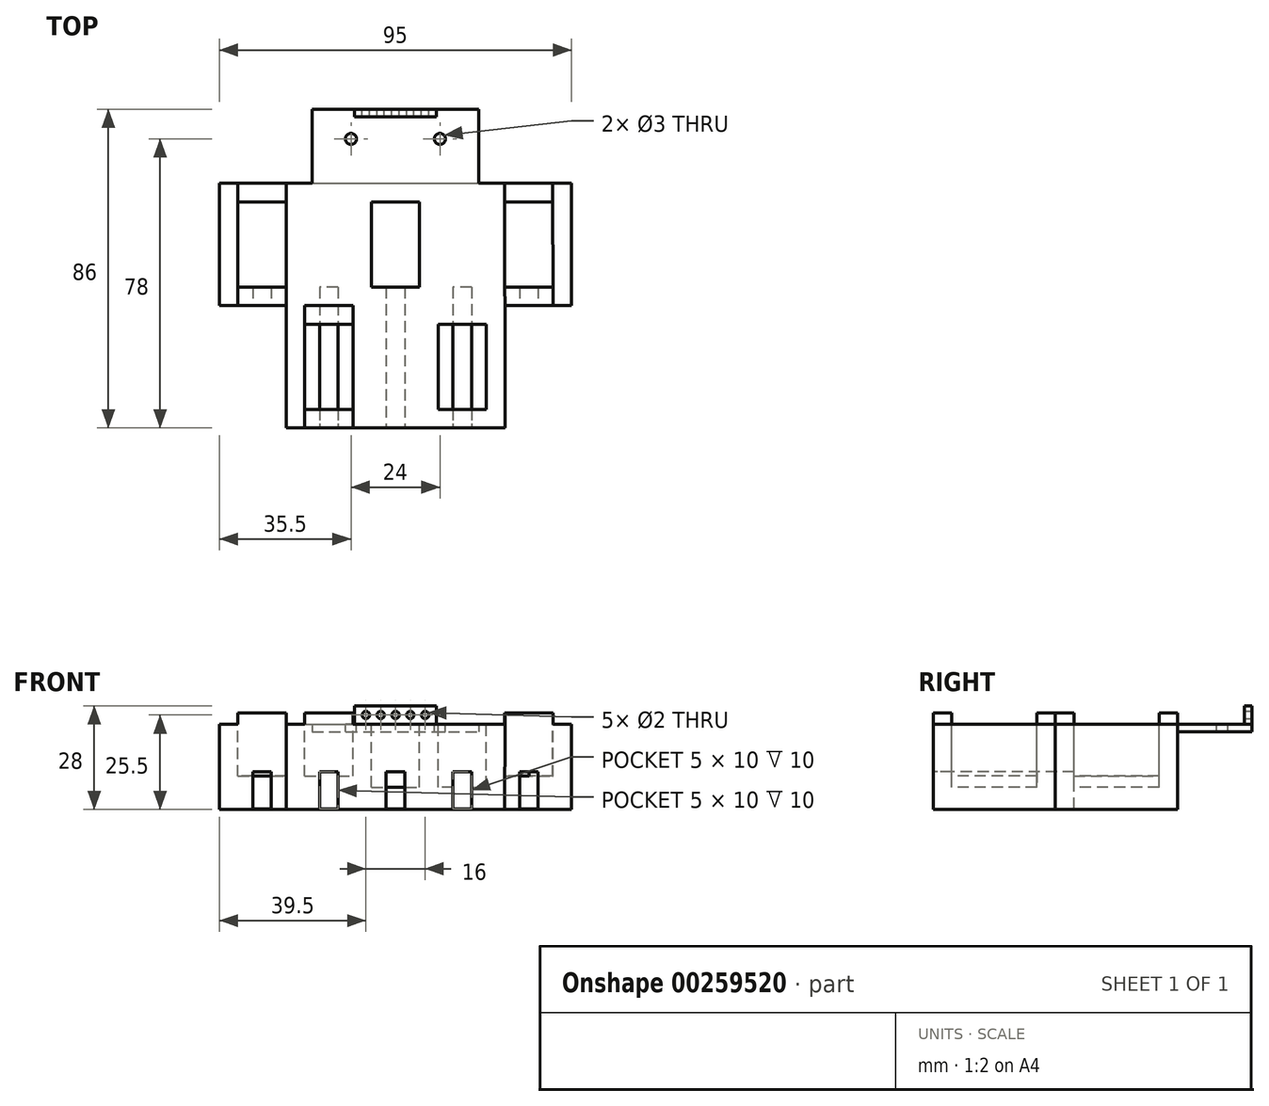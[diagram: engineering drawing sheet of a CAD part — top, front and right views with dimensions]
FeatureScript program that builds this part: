
annotation { "Feature Type Name" : "Feature", "Feature Type Description" : "" }
export const myFeature = defineFeature(function(context is Context, id is Id, definition is map)
    precondition{}
    {
        {
            var Q0;
            Q0=qCreatedBy(makeId("Front.planeOp"),FACE);
            var sketch = newSketch(context, id + "F0", { "sketchPlane" : qUnion([Q0])});
            skLineSegment(sketch, "E0", {"start": v(25, 8) * mm, "end": v(25, -8) * mm});
            skLineSegment(sketch, "E1", {"start": v(25, -8) * mm, "end": v(-25, -8) * mm});
            skLineSegment(sketch, "E2", {"start": v(-25, -8) * mm, "end": v(-25, 8) * mm});
            skLineSegment(sketch, "E3", {"start": v(-25, 8) * mm, "end": v(25, 8) * mm});
            skSolve(sketch);
        }
        {
            var Q0;
            Q0 = qSketchRegion(id + "F0", true);
            extrude(context, id + "F1", {"entities" : qUnion([Q0]), "depth" : 4 * mm});
        }
        {
            var Q0;
            Q0=makeQuery(id+"F1.opExtrude","CAP_FACE",FACE,{"disambiguationData":[OSD([sQuery(id+"F0.wireOp",EDGE,"E0"),sQuery(id+"F0.wireOp",EDGE,"E1"),sQuery(id+"F0.wireOp",EDGE,"E2"),sQuery(id+"F0.wireOp",EDGE,"E3")])],"isStart":false});
            var sketch = newSketch(context, id + "F2", { "sketchPlane" : qUnion([Q0])});
            skLineSegment(sketch, "E4.bottom", {"start": v(-47.5, -11.5) * mm, "end": v(47.5, -11.5) * mm});
            skLineSegment(sketch, "E4.top", {"start": v(-47.5, 11.5) * mm, "end": v(47.5, 11.5) * mm});
            skLineSegment(sketch, "E4.left", {"start": v(-47.5, -11.5) * mm, "end": v(-47.5, 11.5) * mm});
            skLineSegment(sketch, "E4.right", {"start": v(47.5, -11.5) * mm, "end": v(47.5, 11.5) * mm});
            skPoint(sketch, "E4.middle", {"position": v(0, 0) * mm});
            skSolve(sketch);
        }
        {
            var Q0;
            Q0 = qSketchRegion(id + "F2", true);
            extrude(context, id + "F3", {"entities" : qUnion([Q0]), "operationType" : NewBodyOperationType.ADD, "depth" : 33 * mm});
        }
        {
            var Q0;
            Q0=makeQuery(id+"F3.opExtrude","SWEPT_FACE",FACE,{"disambiguationData":[OSD([sQuery(id+"F2.wireOp",EDGE,"E4.top")])]});
            var sketch = newSketch(context, id + "F4", { "sketchPlane" : qUnion([Q0])});
            skPoint(sketch, "E5.trimOffspring.end.orphan", {"position": v(47.5, -20.5) * mm});
            skPoint(sketch, "E6.end.orphan", {"position": v(0, -37) * mm});
            skPoint(sketch, "E6.start.orphan", {"position": v(0, -4) * mm});
            skPoint(sketch, "E7.start.orphan", {"position": v(0, -20.5) * mm});
            skLineSegment(sketch, "E8", {"start": v(6.5, -32) * mm, "end": v(6.5, -9) * mm});
            skLineSegment(sketch, "E9", {"start": v(-6.5, -9) * mm, "end": v(-6.5, -32) * mm});
            skLineSegment(sketch, "E10", {"start": v(-6.5, -9) * mm, "end": v(6.5, -9) * mm});
            skLineSegment(sketch, "E11", {"start": v(-6.5, -32) * mm, "end": v(6.5, -32) * mm});
            skLineSegment(sketch, "E12", {"start": v(42.38, -9) * mm, "end": v(42.48, -31.97) * mm});
            skLineSegment(sketch, "E13", {"start": v(29.5, -22.55) * mm, "end": v(29.5, -9) * mm});
            skPoint(sketch, "E13.endSnap0", {"position": v(0, -9) * mm});
            skLineSegment(sketch, "E14", {"start": v(29.5, -22.55) * mm, "end": v(29.5, -32.03) * mm});
            skLineSegment(sketch, "E15", {"start": v(29.5, -9) * mm, "end": v(42.38, -9) * mm});
            skPoint(sketch, "E16.endSnap0", {"position": v(0, -32) * mm});
            skLineSegment(sketch, "E17", {"start": v(36, -32) * mm, "end": v(29.5, -32.03) * mm});
            skLineSegment(sketch, "E18", {"start": v(29.5, -32.03) * mm, "end": v(42.48, -31.97) * mm});
            skLineSegment(sketch, "E19", {"start": v(-35.27, -9) * mm, "end": v(-42.5, -9) * mm});
            skLineSegment(sketch, "E20", {"start": v(-42.5, -9) * mm, "end": v(-29.5, -9) * mm});
            skLineSegment(sketch, "E21", {"start": v(-29.5, -21.95) * mm, "end": v(-29.5, -9) * mm});
            skLineSegment(sketch, "E22", {"start": v(-35.5, -32) * mm, "end": v(-29.5, -32) * mm});
            skLineSegment(sketch, "E23", {"start": v(-35.5, -32) * mm, "end": v(-42.5, -32) * mm});
            skLineSegment(sketch, "E24", {"start": v(-42.5, -32) * mm, "end": v(-42.5, -21.71) * mm});
            skLineSegment(sketch, "E25", {"start": v(-42.5, -21.71) * mm, "end": v(-42.5, -9) * mm});
            skLineSegment(sketch, "E26", {"start": v(-29.5, -21.95) * mm, "end": v(-29.5, -32) * mm});
            skSolve(sketch);
        }
        {
            var Q0;
            Q0=makeQuery(id+"F4.imprint","IMPRINT",FACE,{"disambiguationData":[TD([[makeQuery(id+"F4.imprint","IMPRINT",EDGE,{"derivedFrom":sQuery(id+"F4.wireOp",EDGE,"E8")}),1.0]])]});
            extrude(context, id + "F5", {"entities" : qUnion([Q0]), "operationType" : NewBodyOperationType.REMOVE, "oppositeDirection" : true, "depth" : 17 * mm});
        }
        {
            var Q0;
            {var subQ0=sQuery(id+"F4.wireOp",EDGE,"E21");Q0=makeQuery(id+"F4.imprint","IMPRINT",FACE,{"disambiguationData":[TD([[makeQuery(id+"F4.imprint","IMPRINT",EDGE,{"derivedFrom":subQ0}),1.0]])]});}
            extrude(context, id + "F6", {"entities" : qUnion([Q0]), "operationType" : NewBodyOperationType.REMOVE, "oppositeDirection" : true, "depth" : 14 * mm});
        }
        {
            var Q0;
            {var subQ1=sQuery(id+"F4.wireOp",EDGE,"E12");Q0=makeQuery(id+"F4.imprint","IMPRINT",FACE,{"disambiguationData":[TD([[makeQuery(id+"F4.imprint","IMPRINT",EDGE,{"derivedFrom":subQ1}),-1.0]])]});}
            extrude(context, id + "F7", {"entities" : qUnion([Q0]), "operationType" : NewBodyOperationType.REMOVE, "oppositeDirection" : true, "depth" : 14 * mm});
        }
        {
            var Q0;
            Q0=makeQuery(id+"F3.opExtrude","SWEPT_FACE",FACE,{"disambiguationData":[OSD([sQuery(id+"F2.wireOp",EDGE,"E4.top")])]});
            var sketch = newSketch(context, id + "F8", { "sketchPlane" : qUnion([Q0])});
            skLineSegment(sketch, "E27", {"start": v(-29.5, -9) * mm, "end": v(-29.5, -4) * mm});
            skLineSegment(sketch, "E28", {"start": v(-42.5, -9) * mm, "end": v(-42.5, -4) * mm});
            skLineSegment(sketch, "E29", {"start": v(-29.5, -32) * mm, "end": v(-29.5, -37) * mm});
            skLineSegment(sketch, "E30", {"start": v(-42.5, -32) * mm, "end": v(-42.5, -37) * mm});
            skLineSegment(sketch, "E31", {"start": v(29.5, -9) * mm, "end": v(29.5, -4) * mm});
            skLineSegment(sketch, "E32", {"start": v(42.38, -9) * mm, "end": v(42.38, -4) * mm});
            skLineSegment(sketch, "E33", {"start": v(29.5, -32.03) * mm, "end": v(29.52, -37) * mm});
            skLineSegment(sketch, "E34", {"start": v(42.48, -31.97) * mm, "end": v(42.5, -37) * mm});
            skSolve(sketch);
        }
        {
            var Q0;
            {var subQ0=sQuery(id+"F8.wireOp",EDGE,"E27");Q0=makeQuery(id+"F8.imprint","IMPRINT",FACE,{"disambiguationData":[TD([[makeQuery(id+"F8.imprint","IMPRINT",EDGE,{"derivedFrom":subQ0}),1.0]])]});}
            var Q1;
            {var subQ0=sQuery(id+"F8.wireOp",EDGE,"E29");Q1=makeQuery(id+"F8.imprint","IMPRINT",FACE,{"disambiguationData":[TD([[makeQuery(id+"F8.imprint","IMPRINT",EDGE,{"derivedFrom":subQ0}),-1.0]])]});}
            var Q2;
            {var subQ0=sQuery(id+"F8.wireOp",EDGE,"E31");Q2=makeQuery(id+"F8.imprint","IMPRINT",FACE,{"disambiguationData":[TD([[makeQuery(id+"F8.imprint","IMPRINT",EDGE,{"derivedFrom":subQ0}),-1.0]])]});}
            var Q3;
            {var subQ0=sQuery(id+"F8.wireOp",EDGE,"E33");Q3=makeQuery(id+"F8.imprint","IMPRINT",FACE,{"disambiguationData":[TD([[makeQuery(id+"F8.imprint","IMPRINT",EDGE,{"derivedFrom":subQ0}),1.0]])]});}
            extrude(context, id + "F9", {"entities" : qUnion([Q0, Q1, Q2, Q3]), "operationType" : NewBodyOperationType.ADD, "depth" : 3 * mm});
        }
        {
            var Q0;
            Q0=makeQuery(id+"F1.opExtrude","CAP_FACE",FACE,{"disambiguationData":[OSD([sQuery(id+"F0.wireOp",EDGE,"E0"),sQuery(id+"F0.wireOp",EDGE,"E1"),sQuery(id+"F0.wireOp",EDGE,"E2"),sQuery(id+"F0.wireOp",EDGE,"E3")])],"isStart":true});
            var sketch = newSketch(context, id + "F10", { "sketchPlane" : qUnion([Q0])});
            skLineSegment(sketch, "E35.0.0", {"start": v(25, 8) * mm, "end": v(-25, 8) * mm});
            skLineSegment(sketch, "E35.0.1", {"start": v(-25, 8) * mm, "end": v(-25, -8) * mm});
            skLineSegment(sketch, "E35.0.2", {"start": v(-25, -8) * mm, "end": v(25, -8) * mm});
            skLineSegment(sketch, "E35.0.3", {"start": v(25, -8) * mm, "end": v(25, 8) * mm});
            skSolve(sketch);
        }
        {
            var Q0;
            Q0=makeQuery(id+"F10.imprint","IMPRINT",FACE,{"disambiguationData":[TD([[makeQuery(id+"F10.imprint","IMPRINT",EDGE,{"derivedFrom":sQuery(id+"F10.wireOp",EDGE,"E35.0.0")}),1.0]])]});
            var Q1;
            {var subQ0=sQuery(id+"F2.wireOp",EDGE,"E4.top");var subQ1=makeQuery(id+"F3.opExtrude","CAP_EDGE",EDGE,{"disambiguationData":[OSD([subQ0])],"isStart":true});Q1=makeQuery(id+"F9.boolean.opBoolean","MERGE",FACE,{"derivedFrom":[makeQuery(id+"F3.opExtrude","CAP_FACE",FACE,{"disambiguationData":[OSD([sQuery(id+"F2.wireOp",EDGE,"E4.bottom"),subQ0,sQuery(id+"F2.wireOp",EDGE,"E4.left"),sQuery(id+"F2.wireOp",EDGE,"E4.right")])],"isStart":true}),makeQuery(id+"F9.opExtrude","SWEPT_FACE",FACE,{"disambiguationData":[OSD([subQ0]),TDD([makeQuery(id+"F8.imprint","IMPRINT",EDGE,{"disambiguationData":[TD([[makeQuery(id+"F8.imprint","INTERSECT",VERTEX,{"derivedFrom":[subQ1,sQuery(id+"F8.wireOp",EDGE,"E27")]}),1.0]])],"derivedFrom":subQ1})])]}),makeQuery(id+"F9.opExtrude","SWEPT_FACE",FACE,{"disambiguationData":[OSD([subQ0]),TDD([makeQuery(id+"F8.imprint","IMPRINT",EDGE,{"disambiguationData":[TD([[makeQuery(id+"F8.imprint","INTERSECT",VERTEX,{"derivedFrom":[subQ1,sQuery(id+"F8.wireOp",EDGE,"E31")]}),-1.0]])],"derivedFrom":subQ1})])]})]});}
            extrude(context, id + "F11", {"entities" : qUnion([Q0]), "operationType" : NewBodyOperationType.REMOVE, "endBound" : BoundingType.UP_TO_SURFACE, "oppositeDirection" : true, "endBoundEntityFace" : qUnion([Q1]), "depth" : 25 * mm});
        }
        {
            var Q0;
            {var subQ0=sQuery(id+"F2.wireOp",EDGE,"E4.right");var subQ1=sQuery(id+"F2.wireOp",EDGE,"E4.left");var subQ2=sQuery(id+"F2.wireOp",EDGE,"E4.top");var subQ3=sQuery(id+"F2.wireOp",EDGE,"E4.bottom");var subQ4=makeQuery(id+"F3.opExtrude","CAP_EDGE",EDGE,{"disambiguationData":[OSD([subQ2])],"isStart":true});Q0=makeQuery(id+"F11.boolean.opBoolean","MERGE",FACE,{"derivedFrom":[makeQuery(id+"F9.boolean.opBoolean","MERGE",FACE,{"derivedFrom":[makeQuery(id+"F3.opExtrude","CAP_FACE",FACE,{"disambiguationData":[OSD([subQ3,subQ2,subQ1,subQ0])],"isStart":true}),makeQuery(id+"F9.opExtrude","SWEPT_FACE",FACE,{"disambiguationData":[OSD([subQ2]),TDD([makeQuery(id+"F8.imprint","IMPRINT",EDGE,{"disambiguationData":[TD([[makeQuery(id+"F8.imprint","INTERSECT",VERTEX,{"derivedFrom":[subQ4,sQuery(id+"F8.wireOp",EDGE,"E27")]}),1.0]])],"derivedFrom":subQ4})])]}),makeQuery(id+"F9.opExtrude","SWEPT_FACE",FACE,{"disambiguationData":[OSD([subQ2]),TDD([makeQuery(id+"F8.imprint","IMPRINT",EDGE,{"disambiguationData":[TD([[makeQuery(id+"F8.imprint","INTERSECT",VERTEX,{"derivedFrom":[subQ4,sQuery(id+"F8.wireOp",EDGE,"E31")]}),-1.0]])],"derivedFrom":subQ4})])]})]}),makeQuery(id+"F11.opExtrude","CAP_FACE",FACE,{"disambiguationData":[OSD([subQ3,subQ2,subQ1,subQ0])],"isStart":false})]});}
            var sketch = newSketch(context, id + "F12", { "sketchPlane" : qUnion([Q0])});
            skLineSegment(sketch, "E36", {"start": v(0, -11.5) * mm, "end": v(22.5, -11.5) * mm});
            skLineSegment(sketch, "E37", {"start": v(0, -11.5) * mm, "end": v(-22.5, -11.5) * mm});
            skLineSegment(sketch, "E38", {"start": v(-22.5, -11.5) * mm, "end": v(-22.5, -9.5) * mm});
            skLineSegment(sketch, "E39", {"start": v(22.5, -11.5) * mm, "end": v(22.5, -9.5) * mm});
            skLineSegment(sketch, "E40", {"start": v(22.5, -9.5) * mm, "end": v(-22.5, -9.5) * mm});
            skLineSegment(sketch, "E41.MirrorCS", {"start": v(22.5, 9.5) * mm, "end": v(-22.5, 9.5) * mm});
            skLineSegment(sketch, "E42.MirrorCS", {"start": v(0, 11.5) * mm, "end": v(22.5, 11.5) * mm});
            skLineSegment(sketch, "E43.MirrorCS", {"start": v(22.5, 11.5) * mm, "end": v(22.5, 9.5) * mm});
            skLineSegment(sketch, "E44.MirrorCS", {"start": v(0, 11.5) * mm, "end": v(-22.5, 11.5) * mm});
            skLineSegment(sketch, "E45.MirrorCS", {"start": v(-22.5, 11.5) * mm, "end": v(-22.5, 9.5) * mm});
            skSolve(sketch);
        }
        {
            var Q0;
            Q0=makeQuery(id+"F12.imprint","IMPRINT",FACE,{"disambiguationData":[TD([[makeQuery(id+"F12.imprint","IMPRINT",EDGE,{"derivedFrom":sQuery(id+"F12.wireOp",EDGE,"E41.MirrorCS")}),-1.0]])]});
            extrude(context, id + "F13", {"entities" : qUnion([Q0]), "operationType" : NewBodyOperationType.ADD, "depth" : 20 * mm});
        }
        {
            var Q0;
            {var subQ0=sQuery(id+"F2.wireOp",EDGE,"E4.top");var subQ1=makeQuery(id+"F3.opExtrude","CAP_EDGE",EDGE,{"disambiguationData":[OSD([subQ0])],"isStart":false});Q0=makeQuery(id+"F9.boolean.opBoolean","MERGE",FACE,{"derivedFrom":[makeQuery(id+"F3.opExtrude","CAP_FACE",FACE,{"disambiguationData":[OSD([sQuery(id+"F2.wireOp",EDGE,"E4.bottom"),subQ0,sQuery(id+"F2.wireOp",EDGE,"E4.left"),sQuery(id+"F2.wireOp",EDGE,"E4.right")])],"isStart":false}),makeQuery(id+"F9.opExtrude","SWEPT_FACE",FACE,{"disambiguationData":[OSD([subQ0]),TDD([makeQuery(id+"F8.imprint","IMPRINT",EDGE,{"disambiguationData":[TD([[makeQuery(id+"F8.imprint","INTERSECT",VERTEX,{"derivedFrom":[subQ1,sQuery(id+"F8.wireOp",EDGE,"E29")]}),1.0]])],"derivedFrom":subQ1})])]}),makeQuery(id+"F9.opExtrude","SWEPT_FACE",FACE,{"disambiguationData":[OSD([subQ0]),TDD([makeQuery(id+"F8.imprint","IMPRINT",EDGE,{"disambiguationData":[TD([[makeQuery(id+"F8.imprint","INTERSECT",VERTEX,{"derivedFrom":[subQ1,sQuery(id+"F8.wireOp",EDGE,"E33")]}),-1.0]])],"derivedFrom":subQ1})])]})]});}
            var sketch = newSketch(context, id + "F14", { "sketchPlane" : qUnion([Q0])});
            skLineSegment(sketch, "E46", {"start": v(0, -11.5) * mm, "end": v(-29.5, -11.5) * mm});
            skLineSegment(sketch, "E47", {"start": v(0, -11.5) * mm, "end": v(29.5, -11.5) * mm});
            skLineSegment(sketch, "E48", {"start": v(-29.5, -11.5) * mm, "end": v(-29.5, 11.5) * mm});
            skLineSegment(sketch, "E49", {"start": v(29.5, -11.5) * mm, "end": v(29.52, 11.5) * mm});
            skSolve(sketch);
        }
        {
            var Q0;
            Q0=makeQuery(id+"F14.imprint","IMPRINT",FACE,{"disambiguationData":[TD([[makeQuery(id+"F14.imprint","IMPRINT",EDGE,{"derivedFrom":sQuery(id+"F14.wireOp",EDGE,"E46")}),1.0]])]});
            extrude(context, id + "F15", {"entities" : qUnion([Q0]), "operationType" : NewBodyOperationType.ADD, "depth" : 33 * mm});
        }
        {
            var Q0;
            {var subQ0=sQuery(id+"F2.wireOp",EDGE,"E4.top");Q0=makeQuery(id+"F15.boolean.opBoolean","MERGE",FACE,{"derivedFrom":[makeQuery(id+"F9.boolean.opBoolean","SPLIT",FACE,{"disambiguationData":[TD([makeQuery(id+"F5.boolean.opBoolean","COPY",FACE,{"derivedFrom":makeQuery(id+"F5.opExtrude","SWEPT_FACE",FACE,{"disambiguationData":[OSD([sQuery(id+"F4.wireOp",EDGE,"E8")])]})})])],"derivedFrom":makeQuery(id+"F3.opExtrude","SWEPT_FACE",FACE,{"disambiguationData":[OSD([subQ0])]})}),makeQuery(id+"F15.opExtrude","SWEPT_FACE",FACE,{"disambiguationData":[OSD([subQ0])]})]});}
            var sketch = newSketch(context, id + "F16", { "sketchPlane" : qUnion([Q0])});
            skLineSegment(sketch, "E50", {"start": v(-17.67, -65) * mm, "end": v(-24.5, -65) * mm});
            skLineSegment(sketch, "E51", {"start": v(-17.67, -65) * mm, "end": v(-11.5, -65) * mm});
            skLineSegment(sketch, "E52", {"start": v(-11.5, -54.94) * mm, "end": v(-11.5, -65) * mm});
            skLineSegment(sketch, "E53", {"start": v(-24.5, -55.7) * mm, "end": v(-24.5, -65) * mm});
            skLineSegment(sketch, "E54", {"start": v(-18.18, -42) * mm, "end": v(-24.5, -42) * mm});
            skLineSegment(sketch, "E55", {"start": v(-18.18, -42) * mm, "end": v(-11.5, -42) * mm});
            skLineSegment(sketch, "E56", {"start": v(-11.5, -54.94) * mm, "end": v(-11.5, -42) * mm});
            skLineSegment(sketch, "E57", {"start": v(-24.5, -55.7) * mm, "end": v(-24.5, -42) * mm});
            skLineSegment(sketch, "E58", {"start": v(17.15, -42) * mm, "end": v(11.5, -42) * mm});
            skLineSegment(sketch, "E59", {"start": v(17.15, -42) * mm, "end": v(24.52, -42) * mm});
            skLineSegment(sketch, "E60", {"start": v(19.42, -65) * mm, "end": v(11.5, -65) * mm});
            skLineSegment(sketch, "E61", {"start": v(19.42, -65) * mm, "end": v(24.52, -65) * mm});
            skLineSegment(sketch, "E62", {"start": v(11.5, -54.94) * mm, "end": v(11.5, -65) * mm});
            skLineSegment(sketch, "E63", {"start": v(24.52, -53.5) * mm, "end": v(24.52, -65) * mm});
            skLineSegment(sketch, "E64", {"start": v(11.5, -54.94) * mm, "end": v(11.5, -42) * mm});
            skLineSegment(sketch, "E65", {"start": v(24.52, -53.5) * mm, "end": v(24.52, -42) * mm});
            skPoint(sketch, "E66.start.orphan", {"position": v(29.52, -53.5) * mm});
            skPoint(sketch, "E67.start.orphan", {"position": v(0, -70) * mm});
            skSolve(sketch);
        }
        {
            var Q0;
            Q0=makeQuery(id+"F16.imprint","IMPRINT",FACE,{"disambiguationData":[TD([[makeQuery(id+"F16.imprint","IMPRINT",EDGE,{"derivedFrom":sQuery(id+"F16.wireOp",EDGE,"E50")}),-1.0]])]});
            extrude(context, id + "F17", {"entities" : qUnion([Q0]), "operationType" : NewBodyOperationType.REMOVE, "oppositeDirection" : true, "depth" : 14 * mm});
        }
        {
            var Q0;
            Q0=makeQuery(id+"F16.imprint","IMPRINT",FACE,{"disambiguationData":[TD([[makeQuery(id+"F16.imprint","IMPRINT",EDGE,{"derivedFrom":sQuery(id+"F16.wireOp",EDGE,"E58")}),1.0]])]});
            extrude(context, id + "F18", {"entities" : qUnion([Q0]), "operationType" : NewBodyOperationType.REMOVE, "oppositeDirection" : true, "depth" : 17 * mm});
        }
        {
            var Q0;
            {var subQ0=sQuery(id+"F2.wireOp",EDGE,"E4.top");Q0=makeQuery(id+"F15.boolean.opBoolean","MERGE",FACE,{"derivedFrom":[makeQuery(id+"F9.boolean.opBoolean","SPLIT",FACE,{"disambiguationData":[TD([makeQuery(id+"F5.boolean.opBoolean","COPY",FACE,{"derivedFrom":makeQuery(id+"F5.opExtrude","SWEPT_FACE",FACE,{"disambiguationData":[OSD([sQuery(id+"F4.wireOp",EDGE,"E8")])]})})])],"derivedFrom":makeQuery(id+"F3.opExtrude","SWEPT_FACE",FACE,{"disambiguationData":[OSD([subQ0])]})}),makeQuery(id+"F15.opExtrude","SWEPT_FACE",FACE,{"disambiguationData":[OSD([subQ0])]})]});}
            var sketch = newSketch(context, id + "F19", { "sketchPlane" : qUnion([Q0])});
            skLineSegment(sketch, "E68", {"start": v(-24.5, -42) * mm, "end": v(-24.5, -37) * mm});
            skLineSegment(sketch, "E69", {"start": v(-24.5, -37) * mm, "end": v(-11.5, -37) * mm});
            skLineSegment(sketch, "E70", {"start": v(-11.5, -37) * mm, "end": v(-11.5, -42) * mm});
            skLineSegment(sketch, "E71", {"start": v(-24.5, -65) * mm, "end": v(-24.5, -70) * mm});
            skLineSegment(sketch, "E72", {"start": v(-11.5, -65) * mm, "end": v(-11.5, -70) * mm});
            skSolve(sketch);
        }
        {
            var Q0;
            {var subQ0=sQuery(id+"F19.wireOp",EDGE,"E71");Q0=makeQuery(id+"F19.imprint","IMPRINT",FACE,{"disambiguationData":[TD([[makeQuery(id+"F19.imprint","IMPRINT",EDGE,{"derivedFrom":subQ0}),1.0]])]});}
            var Q1;
            Q1=makeQuery(id+"F19.imprint","IMPRINT",FACE,{"disambiguationData":[TD([[makeQuery(id+"F19.imprint","IMPRINT",EDGE,{"derivedFrom":sQuery(id+"F19.wireOp",EDGE,"E68")}),-1.0]])]});
            extrude(context, id + "F20", {"entities" : qUnion([Q0, Q1]), "operationType" : NewBodyOperationType.ADD, "depth" : 3 * mm});
        }
        {
            var Q0;
            {var subQ0=sQuery(id+"F2.wireOp",EDGE,"E4.top");Q0=makeQuery(id+"F15.boolean.opBoolean","MERGE",FACE,{"derivedFrom":[makeQuery(id+"F13.boolean.opBoolean","MERGE",FACE,{"derivedFrom":[makeQuery(id+"F9.boolean.opBoolean","SPLIT",FACE,{"disambiguationData":[TD([makeQuery(id+"F5.boolean.opBoolean","COPY",FACE,{"derivedFrom":makeQuery(id+"F5.opExtrude","SWEPT_FACE",FACE,{"disambiguationData":[OSD([sQuery(id+"F4.wireOp",EDGE,"E8")])]})})])],"derivedFrom":makeQuery(id+"F3.opExtrude","SWEPT_FACE",FACE,{"disambiguationData":[OSD([subQ0])]})}),makeQuery(id+"F13.opExtrude","SWEPT_FACE",FACE,{"disambiguationData":[OSD([sQuery(id+"F12.wireOp",EDGE,"E42.MirrorCS"),sQuery(id+"F12.wireOp",EDGE,"E44.MirrorCS")])]})]}),makeQuery(id+"F15.opExtrude","SWEPT_FACE",FACE,{"disambiguationData":[OSD([subQ0])]})]});}
            var sketch = newSketch(context, id + "F21", { "sketchPlane" : qUnion([Q0])});
            skCircle(sketch, "E73", {"center": v(-12, 8) * mm, "radius": 1.5 * mm});
            skCircle(sketch, "E74.MirrorC", {"center": v(12, 8) * mm, "radius": 1.5 * mm});
            skSolve(sketch);
        }
        {
            var Q0;
            Q0 = qSketchRegion(id + "F21", true);
            extrude(context, id + "F22", {"entities" : qUnion([Q0]), "operationType" : NewBodyOperationType.REMOVE, "endBound" : BoundingType.THROUGH_ALL, "oppositeDirection" : true, "depth" : 25 * mm});
        }
        {
            var Q0;
            {var subQ0=sQuery(id+"F2.wireOp",EDGE,"E4.top");Q0=makeQuery(id+"F20.boolean.opBoolean","MERGE",FACE,{"derivedFrom":[makeQuery(id+"F15.opExtrude","CAP_FACE",FACE,{"disambiguationData":[OSD([subQ0,sQuery(id+"F14.wireOp",EDGE,"E46"),sQuery(id+"F14.wireOp",EDGE,"E47"),sQuery(id+"F14.wireOp",EDGE,"E48"),sQuery(id+"F14.wireOp",EDGE,"E49")])],"isStart":false}),makeQuery(id+"F20.opExtrude","SWEPT_FACE",FACE,{"disambiguationData":[OSD([subQ0])]})]});}
            var sketch = newSketch(context, id + "F23", { "sketchPlane" : qUnion([Q0])});
            skLineSegment(sketch, "E75.bottom", {"start": v(-20.5, -1.3) * mm, "end": v(-15.5, -1.3) * mm});
            skLineSegment(sketch, "E75.top", {"start": v(-20.5, -11.3) * mm, "end": v(-15.5, -11.3) * mm});
            skLineSegment(sketch, "E75.left", {"start": v(-20.5, -1.3) * mm, "end": v(-20.5, -11.3) * mm});
            skLineSegment(sketch, "E75.right", {"start": v(-15.5, -1.3) * mm, "end": v(-15.5, -11.3) * mm});
            skPoint(sketch, "E75.middle", {"position": v(-18, -6.3) * mm});
            skPoint(sketch, "E75.middle.positionSnap0", {"position": v(-18, 14.5) * mm});
            skPoint(sketch, "E75.centerSnap0", {"position": v(-18, 14.5) * mm});
            skLineSegment(sketch, "E76.bottom", {"start": v(-2.5, -1.3) * mm, "end": v(2.5, -1.3) * mm});
            skLineSegment(sketch, "E76.top", {"start": v(-2.5, -11.3) * mm, "end": v(2.5, -11.3) * mm});
            skLineSegment(sketch, "E76.left", {"start": v(-2.5, -1.3) * mm, "end": v(-2.5, -11.3) * mm});
            skLineSegment(sketch, "E76.right", {"start": v(2.5, -1.3) * mm, "end": v(2.5, -11.3) * mm});
            skPoint(sketch, "E76.middle", {"position": v(0, -6.3) * mm});
            skPoint(sketch, "E76.middle.positionSnap0", {"position": v(-15.5, -6.3) * mm});
            skPoint(sketch, "E76.centerSnap0", {"position": v(-15.5, -6.3) * mm});
            skLineSegment(sketch, "E77.bottom", {"start": v(15.51, -1.3) * mm, "end": v(20.51, -1.3) * mm});
            skLineSegment(sketch, "E77.top", {"start": v(15.51, -11.3) * mm, "end": v(20.51, -11.3) * mm});
            skLineSegment(sketch, "E77.left", {"start": v(15.51, -1.3) * mm, "end": v(15.51, -11.3) * mm});
            skLineSegment(sketch, "E77.right", {"start": v(20.51, -1.3) * mm, "end": v(20.51, -11.3) * mm});
            skPoint(sketch, "E77.middle", {"position": v(18.01, -6.3) * mm});
            skPoint(sketch, "E77.middle.positionSnap0", {"position": v(18.01, -5.5) * mm});
            skPoint(sketch, "E77.centerSnap0", {"position": v(18.01, -5.5) * mm});
            skLineSegment(sketch, "E78.0.0", {"start": v(-29.5, 14.5) * mm, "end": v(-42.5, 14.5) * mm});
            skLineSegment(sketch, "E78.0.2", {"start": v(-42.5, 14.5) * mm, "end": v(-29.5, 14.5) * mm});
            skLineSegment(sketch, "E79.bottom", {"start": v(-33.5, -1.3) * mm, "end": v(-38.5, -1.3) * mm});
            skLineSegment(sketch, "E79.top", {"start": v(-33.5, -11.3) * mm, "end": v(-38.5, -11.3) * mm});
            skLineSegment(sketch, "E79.left", {"start": v(-33.5, -1.3) * mm, "end": v(-33.5, -11.3) * mm});
            skLineSegment(sketch, "E79.right", {"start": v(-38.5, -1.3) * mm, "end": v(-38.5, -11.3) * mm});
            skPoint(sketch, "E79.middle", {"position": v(-36, -6.3) * mm});
            skPoint(sketch, "E79.middle.positionSnap0", {"position": v(-36, 14.5) * mm});
            skPoint(sketch, "E79.centerSnap0", {"position": v(-36, 14.5) * mm});
            skLineSegment(sketch, "E80.MirrorCS", {"start": v(38.5, -1.3) * mm, "end": v(38.5, -11.3) * mm});
            skLineSegment(sketch, "E81.MirrorCS", {"start": v(33.5, -1.3) * mm, "end": v(38.5, -1.3) * mm});
            skLineSegment(sketch, "E82.MirrorCS", {"start": v(33.5, -1.3) * mm, "end": v(33.5, -11.3) * mm});
            skLineSegment(sketch, "E83.MirrorCS", {"start": v(33.5, -11.3) * mm, "end": v(38.5, -11.3) * mm});
            skPoint(sketch, "E84.0.6.end.orphan", {"position": v(29.52, 11.5) * mm});
            skPoint(sketch, "E84.0.5.end.orphan", {"position": v(29.52, 14.5) * mm});
            skPoint(sketch, "E84.0.1.start.orphan", {"position": v(29.5, -11.5) * mm});
            skPoint(sketch, "E84.0.2.start.orphan", {"position": v(47.5, -11.5) * mm});
            skPoint(sketch, "E84.0.3.start.orphan", {"position": v(47.5, 11.5) * mm});
            skPoint(sketch, "E84.0.4.end.orphan", {"position": v(42.5, 14.5) * mm});
            skPoint(sketch, "E84.0.4.start.orphan", {"position": v(42.5, 11.5) * mm});
            skSolve(sketch);
        }
        {
            var Q0;
            Q0 = qSketchRegion(id + "F23", true);
            var Q1;
            Q1=makeQuery(id+"F5.boolean.opBoolean","COPY",FACE,{"derivedFrom":makeQuery(id+"F5.opExtrude","SWEPT_FACE",FACE,{"disambiguationData":[OSD([sQuery(id+"F4.wireOp",EDGE,"E11")])]})});
            extrude(context, id + "F24", {"entities" : qUnion([Q0]), "operationType" : NewBodyOperationType.REMOVE, "endBound" : BoundingType.UP_TO_SURFACE, "oppositeDirection" : true, "endBoundEntityFace" : qUnion([Q1]), "depth" : 25 * mm});
        }
        {
            var Q0;
            Q0=makeQuery(id+"F13.opExtrude","CAP_FACE",FACE,{"disambiguationData":[OSD([sQuery(id+"F12.wireOp",EDGE,"E41.MirrorCS"),sQuery(id+"F12.wireOp",EDGE,"E42.MirrorCS"),sQuery(id+"F12.wireOp",EDGE,"E43.MirrorCS"),sQuery(id+"F12.wireOp",EDGE,"E44.MirrorCS"),sQuery(id+"F12.wireOp",EDGE,"E45.MirrorCS")])],"isStart":false});
            var sketch = newSketch(context, id + "F25", { "sketchPlane" : qUnion([Q0])});
            skCircle(sketch, "E85", {"center": v(0, 14) * mm, "radius": 1 * mm});
            skCircle(sketch, "E86.1.0.0", {"center": v(4, 14) * mm, "radius": 1 * mm});
            skCircle(sketch, "E86.2.0.0", {"center": v(8, 14) * mm, "radius": 1 * mm});
            skLineSegment(sketch, "E86.direction1", {"start": v(0, 14) * mm, "end": v(4, 14) * mm, "construction": true});
            skCircle(sketch, "E87.MirrorC", {"center": v(-4, 14) * mm, "radius": 1 * mm});
            skCircle(sketch, "E88.MirrorC", {"center": v(-8, 14) * mm, "radius": 1 * mm});
            skLineSegment(sketch, "E89.bottom", {"start": v(-11, 11.5) * mm, "end": v(11, 11.5) * mm});
            skLineSegment(sketch, "E89.top", {"start": v(-11, 16.5) * mm, "end": v(11, 16.5) * mm});
            skLineSegment(sketch, "E89.left", {"start": v(-11, 11.5) * mm, "end": v(-11, 16.5) * mm});
            skLineSegment(sketch, "E89.right", {"start": v(11, 11.5) * mm, "end": v(11, 16.5) * mm});
            skSolve(sketch);
        }
        {
            var Q0;
            Q0=makeQuery(id+"F25.imprint","IMPRINT",FACE,{"disambiguationData":[TD([[makeQuery(id+"F25.imprint","IMPRINT",EDGE,{"derivedFrom":sQuery(id+"F25.wireOp",EDGE,"E85")}),-1.0]])]});
            extrude(context, id + "F26", {"entities" : qUnion([Q0]), "operationType" : NewBodyOperationType.ADD, "oppositeDirection" : true, "depth" : 2 * mm});
        }
    });
